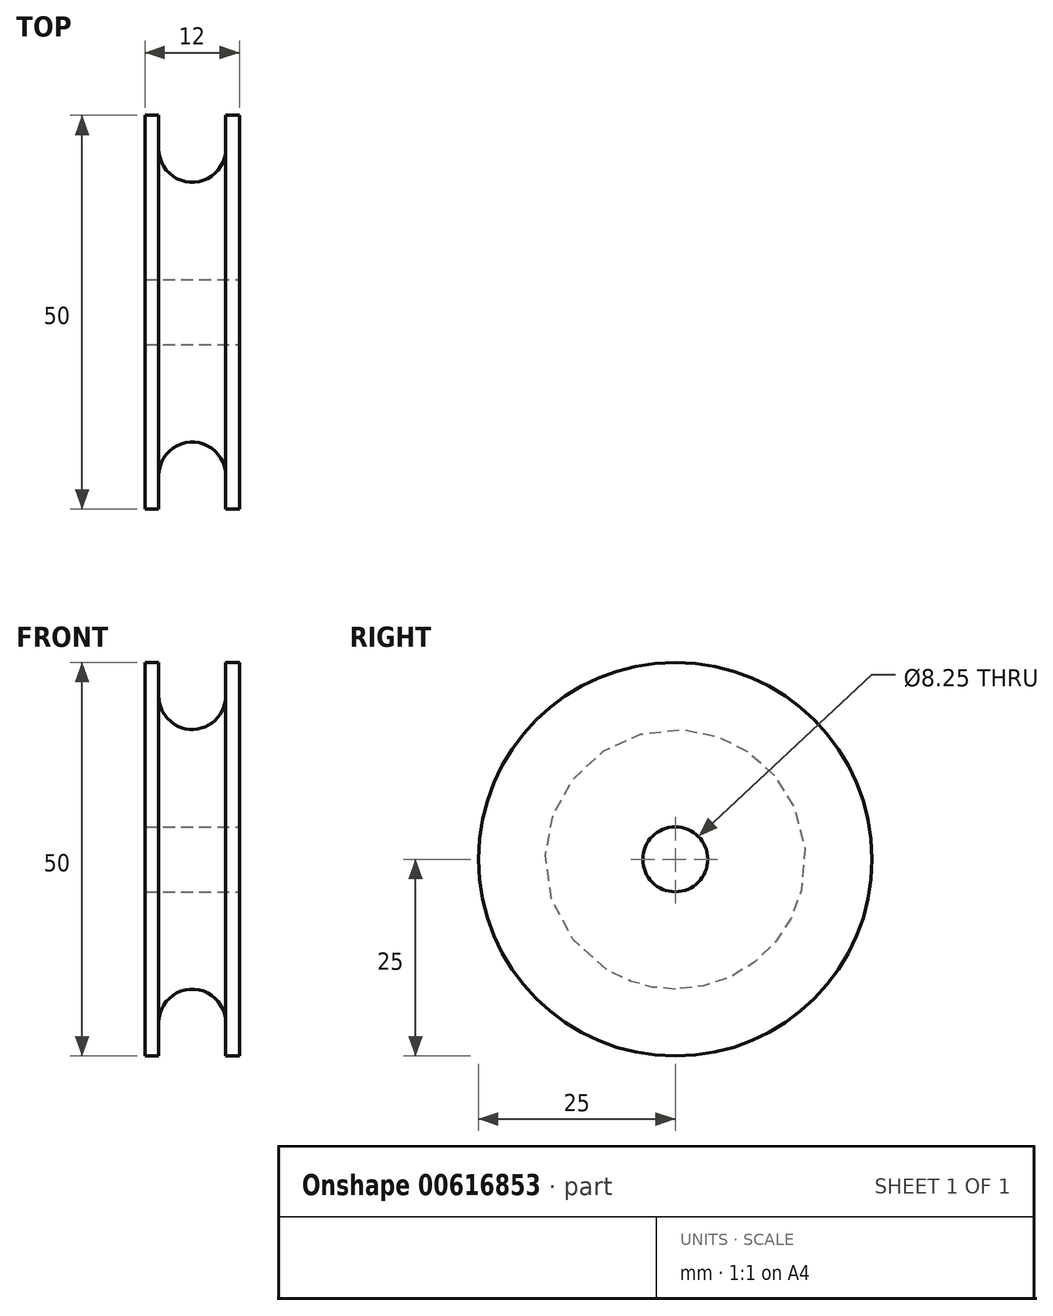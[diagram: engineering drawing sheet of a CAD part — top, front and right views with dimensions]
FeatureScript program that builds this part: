
annotation { "Feature Type Name" : "Feature", "Feature Type Description" : "" }
export const myFeature = defineFeature(function(context is Context, id is Id, definition is map)
    precondition{}
    {
        {
            var Q0;
            Q0=qCreatedBy(makeId("Front.planeOp"),FACE);
            var sketch = newSketch(context, id + "F0", { "sketchPlane" : qUnion([Q0])});
            skLineSegment(sketch, "E0", {"start": v(0, 4.12) * mm, "end": v(-12, 4.12) * mm});
            skLineSegment(sketch, "E1", {"start": v(-12, 4.12) * mm, "end": v(-12, 25) * mm});
            skLineSegment(sketch, "E2", {"start": v(-12, 25) * mm, "end": v(-10.25, 25) * mm});
            skLineSegment(sketch, "E3", {"start": v(-10.25, 25) * mm, "end": v(-10.25, 20.75) * mm});
            skLineSegment(sketch, "E4", {"start": v(0, 4.13) * mm, "end": v(0, 25) * mm});
            skLineSegment(sketch, "E5", {"start": v(0, 25) * mm, "end": v(-1.75, 25) * mm});
            skLineSegment(sketch, "E6", {"start": v(-1.75, 25) * mm, "end": v(-1.75, 20.75) * mm});
            skArc(sketch, "E7", {"start": v(-10.25, 20.75) * mm, "mid": v(-6, 16.5) * mm, "end": v(-1.75, 20.75) * mm});
            skLineSegment(sketch, "E8", {"start": v(0, 0) * mm, "end": v(-18.06, 0) * mm, "construction": true});
            skSolve(sketch);
        }
        {
            var Q0;
            Q0=qSketchRegion(id+"F0",true);
            var Q1;
            Q1=sQuery(id+"F0.wireOp",EDGE,"E8");
            revolve(context, id + "F1", {"surfaceOperationType" : NewSurfaceOperationType.NEW, "entities" : qUnion([Q0]), "axis" : qUnion([Q1]), "revolveType" : RevolveType.FULL});
        }
    });
